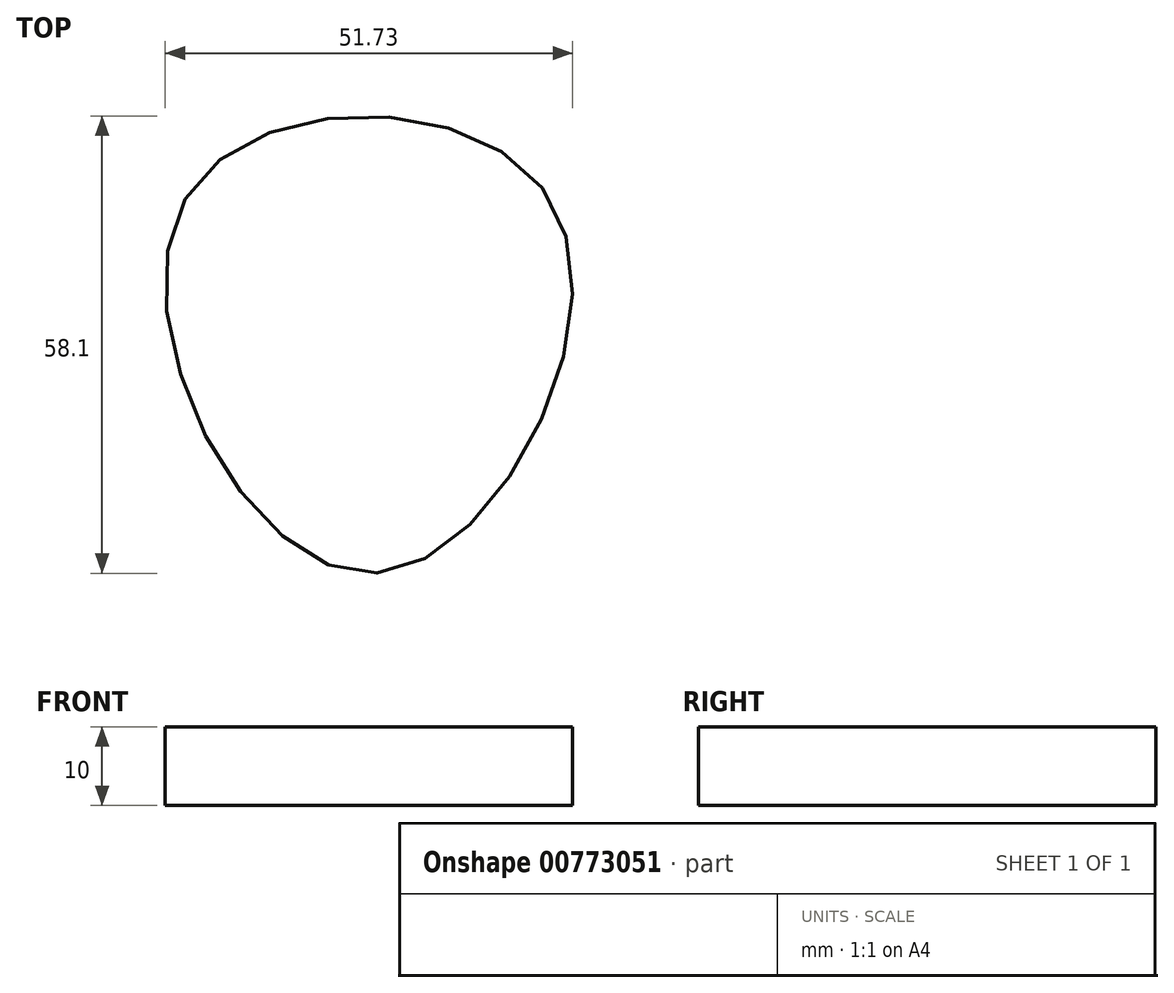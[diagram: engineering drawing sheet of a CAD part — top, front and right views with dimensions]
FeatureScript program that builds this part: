
annotation { "Feature Type Name" : "Feature", "Feature Type Description" : "" }
export const myFeature = defineFeature(function(context is Context, id is Id, definition is map)
    precondition{}
    {
        {
            var Q0;
            Q0=qCreatedBy(makeId("Top.planeOp"),FACE);
            var sketch = newSketch(context, id + "F0", { "sketchPlane" : qUnion([Q0])});
            skFitSpline(sketch, "E0", {"points": [v(-23.94, 19.57) * mm, v(22.84, 18.9) * mm, v(-0.55, -27.96) * mm, v(-23.94, 19.57) * mm]});
            skSolve(sketch);
        }
        {
            var Q0;
            Q0=makeQuery(id+"F0.imprint","IMPRINT",FACE,{"disambiguationData":[TD([[makeQuery(id+"F0.imprint","IMPRINT",EDGE,{"derivedFrom":sQuery(id+"F0.wireOp",EDGE,"E0")}),-1.0]])]});
            extrude(context, id + "F1", {"entities" : qUnion([Q0]), "depth" : 10 * mm, "offsetDistance" : 25.4 * mm});
        }
    });
